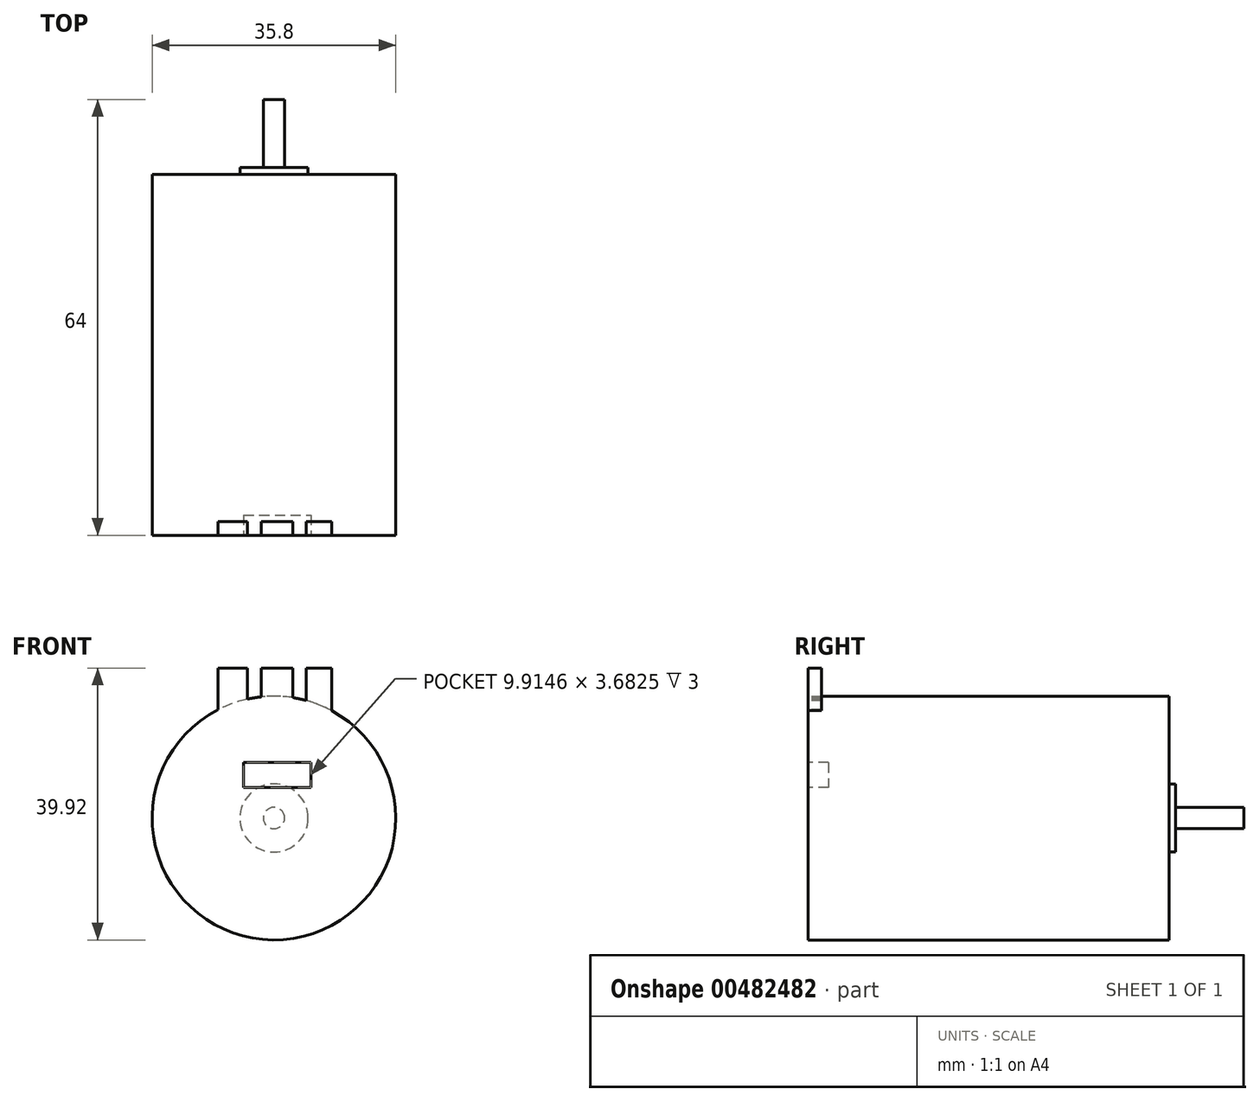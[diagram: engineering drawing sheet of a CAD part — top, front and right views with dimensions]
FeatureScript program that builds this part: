
annotation { "Feature Type Name" : "Feature", "Feature Type Description" : "" }
export const myFeature = defineFeature(function(context is Context, id is Id, definition is map)
    precondition{}
    {
        {
            var Q0;
            Q0=qCreatedBy(makeId("Front.planeOp"),FACE);
            var sketch = newSketch(context, id + "F0", { "sketchPlane" : qUnion([Q0])});
            skCircle(sketch, "E0", {"center": v(-27.2, 20.96) * mm, "radius": 17.9 * mm});
            skSolve(sketch);
        }
        {
            var Q0;
            Q0=makeQuery(id+"F0.imprint","IMPRINT",FACE,{"disambiguationData":[TD([[makeQuery(id+"F0.imprint","IMPRINT",EDGE,{"derivedFrom":sQuery(id+"F0.wireOp",EDGE,"E0")}),1.0]])]});
            extrude(context, id + "F1", {"entities" : qUnion([Q0]), "depth" : 53 * mm, "offsetDistance" : 25 * mm});
        }
        {
            var Q0;
            Q0=makeQuery(id+"F1.opExtrude","CAP_FACE",FACE,{"disambiguationData":[OSD([sQuery(id+"F0.wireOp",EDGE,"E0")])],"isStart":true});
            var sketch = newSketch(context, id + "F2", { "sketchPlane" : qUnion([Q0])});
            skCircle(sketch, "E1", {"center": v(27.2, 20.96) * mm, "radius": 5 * mm});
            skSolve(sketch);
        }
        {
            var Q0;
            Q0 = qSketchRegion(id + "F2", true);
            extrude(context, id + "F3", {"entities" : qUnion([Q0]), "operationType" : NewBodyOperationType.ADD, "depth" : 1 * mm, "offsetDistance" : 25 * mm});
        }
        {
            var Q0;
            Q0=makeQuery(id+"F3.opExtrude","CAP_FACE",FACE,{"disambiguationData":[OSD([sQuery(id+"F2.wireOp",EDGE,"E1")])],"isStart":false});
            var sketch = newSketch(context, id + "F4", { "sketchPlane" : qUnion([Q0])});
            skCircle(sketch, "E2", {"center": v(27.2, 20.96) * mm, "radius": 1.57 * mm});
            skSolve(sketch);
        }
        {
            var Q0;
            Q0=makeQuery(id+"F4.imprint","IMPRINT",FACE,{"disambiguationData":[TD([[makeQuery(id+"F4.imprint","IMPRINT",EDGE,{"derivedFrom":sQuery(id+"F4.wireOp",EDGE,"E2")}),1.0]])]});
            extrude(context, id + "F5", {"entities" : qUnion([Q0]), "operationType" : NewBodyOperationType.ADD, "depth" : 10 * mm, "offsetDistance" : 25 * mm});
        }
        {
            var Q0;
            Q0=makeQuery(id+"F1.opExtrude","CAP_FACE",FACE,{"disambiguationData":[OSD([sQuery(id+"F0.wireOp",EDGE,"E0")])],"isStart":false});
            var sketch = newSketch(context, id + "F6", { "sketchPlane" : qUnion([Q0])});
            skLineSegment(sketch, "E3.bottom", {"start": v(-31.66, 29.1) * mm, "end": v(-21.74, 29.1) * mm});
            skLineSegment(sketch, "E3.top", {"start": v(-31.66, 25.42) * mm, "end": v(-21.74, 25.42) * mm});
            skLineSegment(sketch, "E3.left", {"start": v(-31.66, 29.1) * mm, "end": v(-31.66, 25.42) * mm});
            skLineSegment(sketch, "E3.right", {"start": v(-21.74, 29.1) * mm, "end": v(-21.74, 25.42) * mm});
            skSolve(sketch);
        }
        {
            var Q0;
            Q0=makeQuery(id+"F6.imprint","IMPRINT",FACE,{"disambiguationData":[TD([[makeQuery(id+"F6.imprint","IMPRINT",EDGE,{"derivedFrom":sQuery(id+"F6.wireOp",EDGE,"E3.bottom")}),-1.0]])]});
            extrude(context, id + "F7", {"entities" : qUnion([Q0]), "operationType" : NewBodyOperationType.REMOVE, "oppositeDirection" : true, "depth" : 3 * mm, "offsetDistance" : 25 * mm});
        }
        {
            var Q0;
            Q0=makeQuery(id+"F1.opExtrude","CAP_FACE",FACE,{"disambiguationData":[OSD([sQuery(id+"F0.wireOp",EDGE,"E0")])],"isStart":false});
            var sketch = newSketch(context, id + "F8", { "sketchPlane" : qUnion([Q0])});
            skLineSegment(sketch, "E4", {"start": v(-35.42, 36.86) * mm, "end": v(-35.42, 42.98) * mm});
            skLineSegment(sketch, "E5", {"start": v(-35.42, 42.98) * mm, "end": v(-31.1, 42.98) * mm});
            skLineSegment(sketch, "E6", {"start": v(-18.72, 42.98) * mm, "end": v(-18.72, 36.73) * mm});
            skLineSegment(sketch, "E7", {"start": v(-31.1, 42.98) * mm, "end": v(-31.1, 38.43) * mm});
            skLineSegment(sketch, "E8", {"start": v(-22.45, 42.98) * mm, "end": v(-22.45, 38.22) * mm});
            skLineSegment(sketch, "E9", {"start": v(-29.08, 42.98) * mm, "end": v(-29.08, 38.76) * mm});
            skLineSegment(sketch, "E10", {"start": v(-24.42, 42.98) * mm, "end": v(-24.42, 38.65) * mm});
            skLineSegment(sketch, "E11.trimOffspring", {"start": v(-29.08, 42.98) * mm, "end": v(-24.42, 42.98) * mm});
            skLineSegment(sketch, "E12.trimOffspring", {"start": v(-22.45, 42.98) * mm, "end": v(-18.72, 42.98) * mm});
            skSolve(sketch);
        }
        {
            var Q0;
            {var subQ0=sQuery(id+"F8.wireOp",EDGE,"E4");Q0=makeQuery(id+"F8.imprint","IMPRINT",FACE,{"disambiguationData":[TD([[makeQuery(id+"F8.imprint","IMPRINT",EDGE,{"derivedFrom":subQ0}),-1.0]])]});}
            var Q1;
            {var subQ0=sQuery(id+"F8.wireOp",EDGE,"E9");Q1=makeQuery(id+"F8.imprint","IMPRINT",FACE,{"disambiguationData":[TD([[makeQuery(id+"F8.imprint","IMPRINT",EDGE,{"derivedFrom":subQ0}),1.0]])]});}
            var Q2;
            {var subQ0=sQuery(id+"F8.wireOp",EDGE,"E6");Q2=makeQuery(id+"F8.imprint","IMPRINT",FACE,{"disambiguationData":[TD([[makeQuery(id+"F8.imprint","IMPRINT",EDGE,{"derivedFrom":subQ0}),-1.0]])]});}
            extrude(context, id + "F9", {"entities" : qUnion([Q0, Q1, Q2]), "operationType" : NewBodyOperationType.ADD, "oppositeDirection" : true, "depth" : 2 * mm, "offsetDistance" : 25 * mm});
        }
    });
